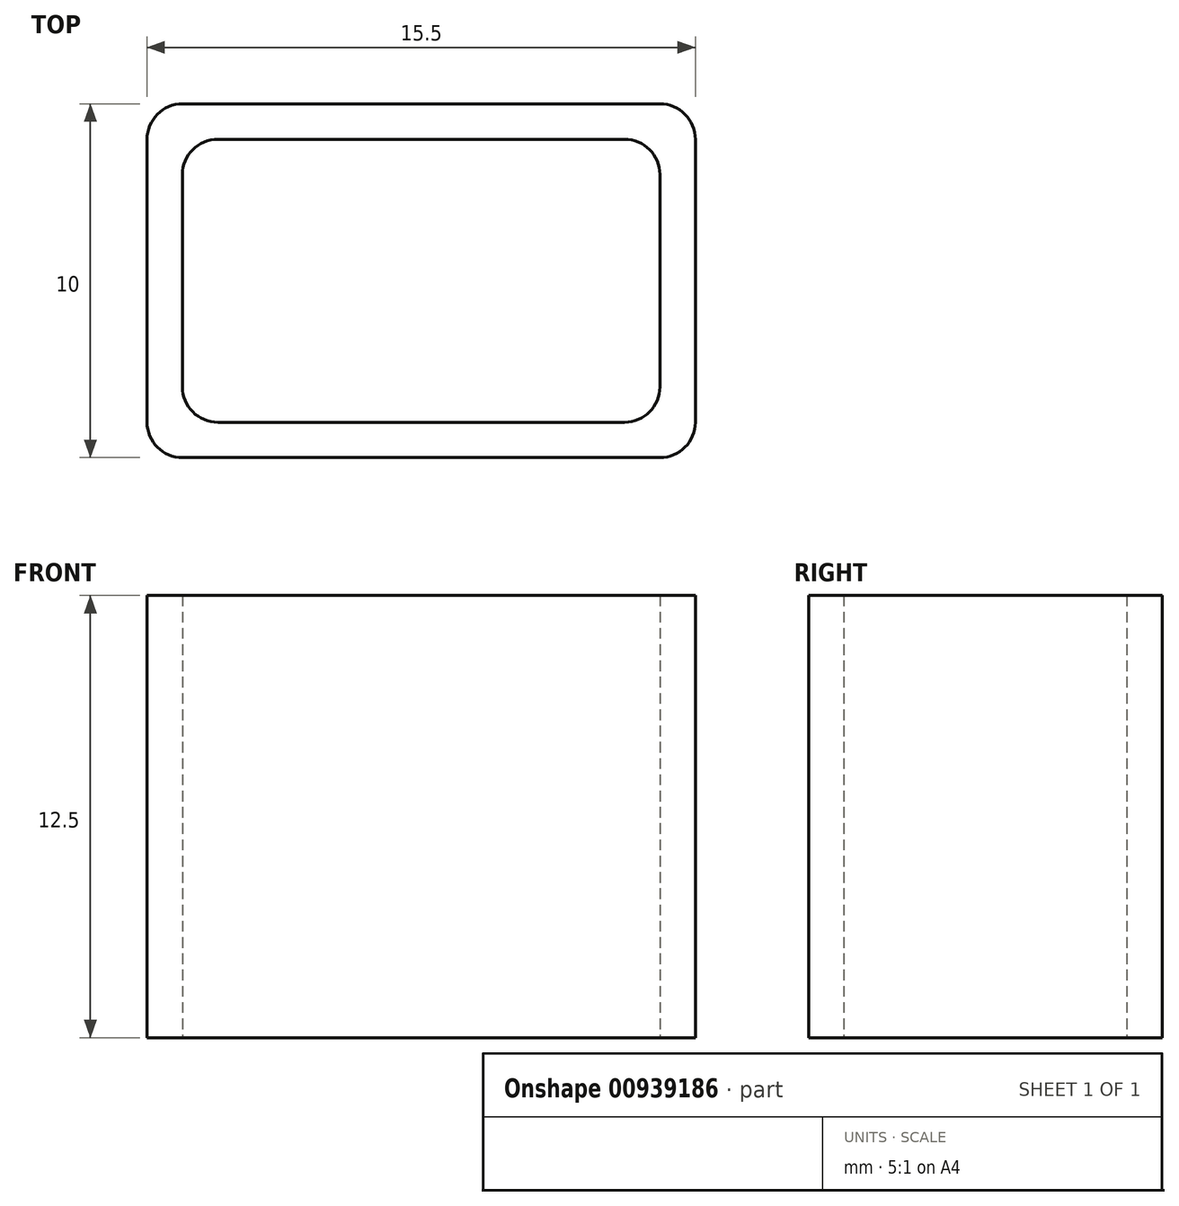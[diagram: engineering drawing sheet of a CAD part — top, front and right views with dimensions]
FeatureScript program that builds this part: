
annotation { "Feature Type Name" : "Feature", "Feature Type Description" : "" }
export const myFeature = defineFeature(function(context is Context, id is Id, definition is map)
    precondition{}
    {
        {
            var Q0;
            Q0=qCreatedBy(makeId("Top.planeOp"),FACE);
            var sketch = newSketch(context, id + "F0", { "sketchPlane" : qUnion([Q0])});
            skLineSegment(sketch, "E0.bottom", {"start": v(-6.75, 5) * mm, "end": v(6.75, 5) * mm});
            skLineSegment(sketch, "E0.top", {"start": v(-6.75, -5) * mm, "end": v(6.75, -5) * mm});
            skLineSegment(sketch, "E0.left", {"start": v(-7.75, 4) * mm, "end": v(-7.75, -4) * mm});
            skLineSegment(sketch, "E0.right", {"start": v(7.75, 4) * mm, "end": v(7.75, -4) * mm});
            skPoint(sketch, "E0.middle", {"position": v(0, 0) * mm});
            skPoint(sketch, "E1.visualSharp", {"position": v(-7.75, 5) * mm});
            skArc(sketch, "E1.filletArc", {"start": v(-6.75, 5) * mm, "mid": v(-7.46, 4.7) * mm, "end": v(-7.75, 4) * mm});
            skPoint(sketch, "E2.visualSharp", {"position": v(7.75, 5) * mm});
            skArc(sketch, "E2.filletArc", {"start": v(7.75, 4) * mm, "mid": v(7.46, 4.7) * mm, "end": v(6.75, 5) * mm});
            skPoint(sketch, "E3.visualSharp", {"position": v(7.75, -5) * mm});
            skArc(sketch, "E3.filletArc", {"start": v(6.75, -5) * mm, "mid": v(7.46, -4.7) * mm, "end": v(7.75, -4) * mm});
            skPoint(sketch, "E4.visualSharp", {"position": v(-7.75, -5) * mm});
            skArc(sketch, "E4.filletArc", {"start": v(-7.75, -4) * mm, "mid": v(-7.46, -4.7) * mm, "end": v(-6.75, -5) * mm});
            skLineSegment(sketch, "E5.bottom", {"start": v(-5.75, 4) * mm, "end": v(5.75, 4) * mm});
            skLineSegment(sketch, "E5.top", {"start": v(-5.75, -4) * mm, "end": v(5.75, -4) * mm});
            skLineSegment(sketch, "E5.left", {"start": v(-6.75, 3) * mm, "end": v(-6.75, -3) * mm});
            skLineSegment(sketch, "E5.right", {"start": v(6.75, 3) * mm, "end": v(6.75, -3) * mm});
            skArc(sketch, "E6.filletArc", {"start": v(-5.75, 4) * mm, "mid": v(-6.46, 3.7) * mm, "end": v(-6.75, 3) * mm});
            skArc(sketch, "E7.filletArc", {"start": v(6.75, 3) * mm, "mid": v(6.46, 3.7) * mm, "end": v(5.75, 4) * mm});
            skArc(sketch, "E8.filletArc", {"start": v(5.75, -4) * mm, "mid": v(6.46, -3.7) * mm, "end": v(6.75, -3) * mm});
            skArc(sketch, "E9.filletArc", {"start": v(-6.75, -3) * mm, "mid": v(-6.46, -3.7) * mm, "end": v(-5.75, -4) * mm});
            skSolve(sketch);
        }
        {
            var Q0;
            Q0=makeQuery(id+"F0.imprint","IMPRINT",FACE,{"disambiguationData":[TD([[makeQuery(id+"F0.imprint","IMPRINT",EDGE,{"derivedFrom":sQuery(id+"F0.wireOp",EDGE,"E0.bottom")}),-1.0]])]});
            extrude(context, id + "F1", {"entities" : qUnion([Q0]), "depth" : 12.5 * mm, "offsetDistance" : 25 * mm});
        }
    });
